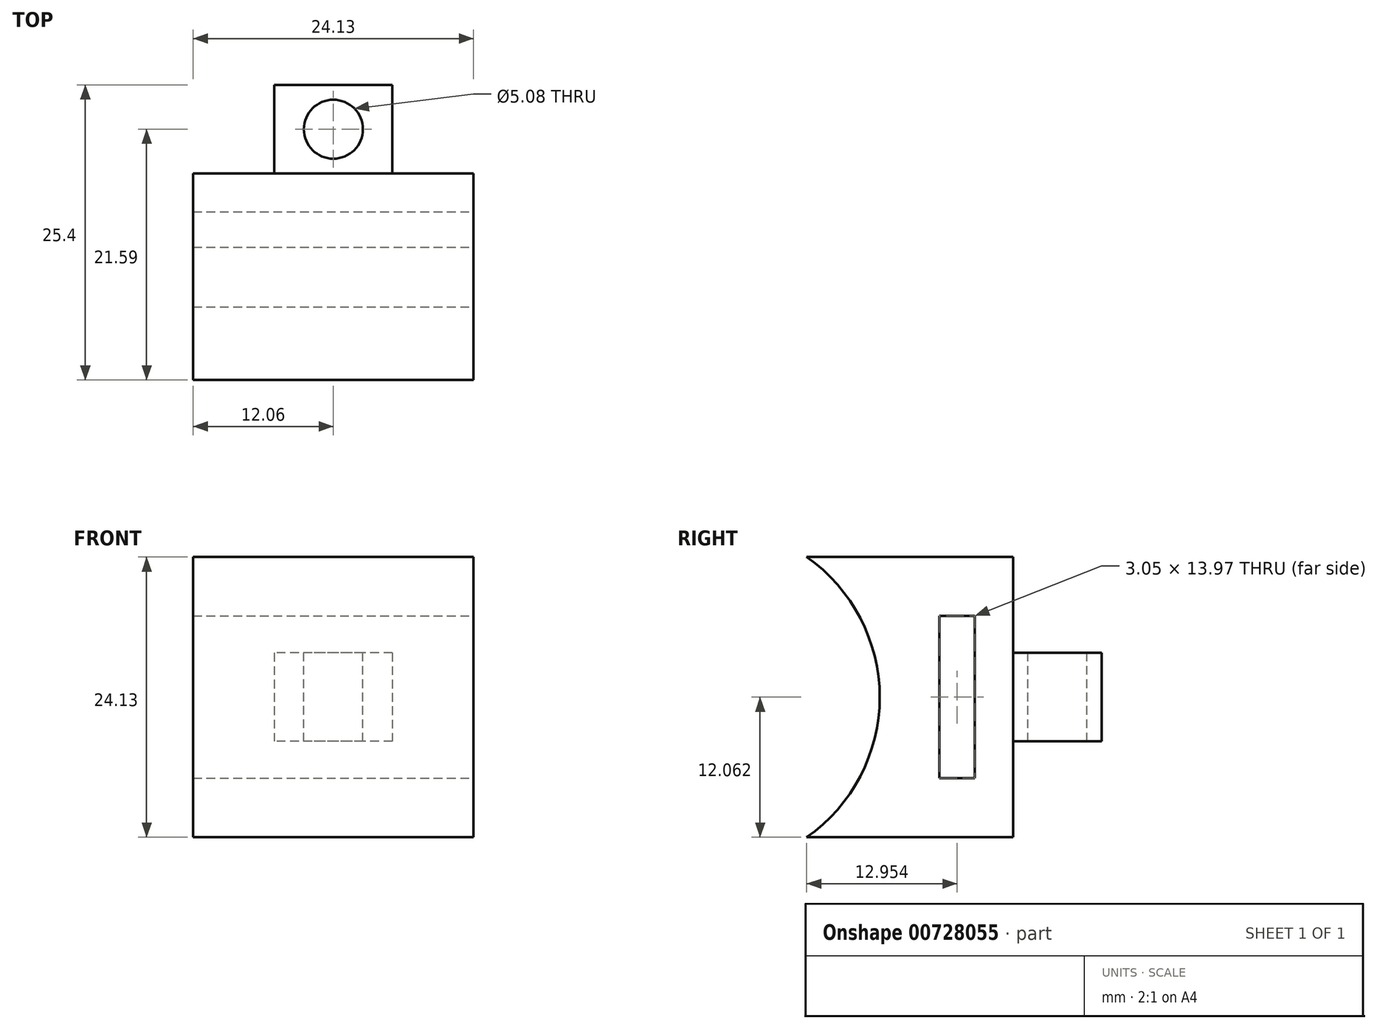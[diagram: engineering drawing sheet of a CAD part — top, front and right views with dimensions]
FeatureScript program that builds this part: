
annotation { "Feature Type Name" : "Feature", "Feature Type Description" : "" }
export const myFeature = defineFeature(function(context is Context, id is Id, definition is map)
    precondition{}
    {
        {
            var Q0;
            Q0=qCreatedBy(makeId("Front.planeOp"),FACE);
            var sketch = newSketch(context, id + "F0", { "sketchPlane" : qUnion([Q0])});
            skLineSegment(sketch, "E0.bottom", {"start": v(-34.91, 42.79) * mm, "end": v(-10.78, 42.79) * mm});
            skLineSegment(sketch, "E0.top", {"start": v(-34.91, 18.66) * mm, "end": v(-10.78, 18.66) * mm});
            skLineSegment(sketch, "E0.left", {"start": v(-34.91, 42.79) * mm, "end": v(-34.91, 18.66) * mm});
            skLineSegment(sketch, "E0.right", {"start": v(-10.78, 42.79) * mm, "end": v(-10.78, 18.66) * mm});
            skSolve(sketch);
        }
        {
            var Q0;
            Q0=makeQuery(id+"F0.imprint","IMPRINT",FACE,{"disambiguationData":[TD([[makeQuery(id+"F0.imprint","IMPRINT",EDGE,{"derivedFrom":sQuery(id+"F0.wireOp",EDGE,"E0.bottom")}),-1.0]])]});
            extrude(context, id + "F1", {"entities" : qUnion([Q0]), "depth" : 17.78 * mm, "offsetDistance" : 25.4 * mm});
        }
        {
            var Q0;
            Q0=makeQuery(id+"F1.opExtrude","SWEPT_FACE",FACE,{"disambiguationData":[OSD([sQuery(id+"F0.wireOp",EDGE,"E0.right")])]});
            var sketch = newSketch(context, id + "F2", { "sketchPlane" : qUnion([Q0])});
            skArc(sketch, "E1", {"start": v(-17.78, 18.66) * mm, "mid": v(-11.5, 30.72) * mm, "end": v(-17.78, 42.79) * mm});
            skSolve(sketch);
        }
        {
            var Q0;
            Q0 = qSketchRegion(id + "F2", true);
            var Q1;
            Q1=makeQuery(id+"F2.imprint","IMPRINT",FACE,{"disambiguationData":[TD([[makeQuery(id+"F2.imprint","IMPRINT",EDGE,{"derivedFrom":sQuery(id+"F2.wireOp",EDGE,"E1")}),1.0]])]});
            extrude(context, id + "F3", {"entities" : qUnion([Q0, Q1]), "operationType" : NewBodyOperationType.REMOVE, "endBound" : BoundingType.THROUGH_ALL, "oppositeDirection" : true, "depth" : 25.4 * mm, "offsetDistance" : 25.4 * mm});
        }
        {
            var Q0;
            Q0=makeQuery(id+"F1.opExtrude","CAP_FACE",FACE,{"disambiguationData":[OSD([sQuery(id+"F0.wireOp",EDGE,"E0.bottom"),sQuery(id+"F0.wireOp",EDGE,"E0.top"),sQuery(id+"F0.wireOp",EDGE,"E0.left"),sQuery(id+"F0.wireOp",EDGE,"E0.right")])],"isStart":true});
            var sketch = newSketch(context, id + "F4", { "sketchPlane" : qUnion([Q0])});
            skLineSegment(sketch, "E2.bottom", {"start": v(17.77, 34.53) * mm, "end": v(27.93, 34.53) * mm});
            skLineSegment(sketch, "E2.top", {"start": v(17.77, 26.91) * mm, "end": v(27.93, 26.91) * mm});
            skLineSegment(sketch, "E2.left", {"start": v(17.77, 34.53) * mm, "end": v(17.77, 26.91) * mm});
            skLineSegment(sketch, "E2.right", {"start": v(27.93, 34.53) * mm, "end": v(27.93, 26.91) * mm});
            skSolve(sketch);
        }
        {
            var Q0;
            Q0 = qSketchRegion(id + "F4", true);
            extrude(context, id + "F5", {"entities" : qUnion([Q0]), "operationType" : NewBodyOperationType.ADD, "depth" : 7.62 * mm, "offsetDistance" : 25.4 * mm});
        }
        {
            var Q0;
            Q0=makeQuery(id+"F5.opExtrude","SWEPT_FACE",FACE,{"disambiguationData":[OSD([sQuery(id+"F4.wireOp",EDGE,"E2.bottom")])]});
            var sketch = newSketch(context, id + "F6", { "sketchPlane" : qUnion([Q0])});
            skCircle(sketch, "E3", {"center": v(-22.85, 3.81) * mm, "radius": 2.54 * mm});
            skPoint(sketch, "E3.first.point", {"position": v(-21.78, 1.5) * mm});
            skPoint(sketch, "E3.second.point", {"position": v(-23.77, 6.18) * mm});
            skPoint(sketch, "E3.third.point", {"position": v(-25.37, 3.49) * mm});
            skSolve(sketch);
        }
        {
            var Q0;
            Q0=makeQuery(id+"F6.imprint","IMPRINT",FACE,{"disambiguationData":[TD([[makeQuery(id+"F6.imprint","IMPRINT",EDGE,{"derivedFrom":sQuery(id+"F6.wireOp",EDGE,"E3")}),1.0]])]});
            extrude(context, id + "F7", {"entities" : qUnion([Q0]), "operationType" : NewBodyOperationType.REMOVE, "endBound" : BoundingType.THROUGH_ALL, "oppositeDirection" : true, "depth" : 25.4 * mm, "offsetDistance" : 25.4 * mm});
        }
        {
            var Q0;
            Q0=makeQuery(id+"F1.opExtrude","SWEPT_FACE",FACE,{"disambiguationData":[OSD([sQuery(id+"F0.wireOp",EDGE,"E0.right")])]});
            var sketch = newSketch(context, id + "F8", { "sketchPlane" : qUnion([Q0])});
            skLineSegment(sketch, "E4.bottom", {"start": v(-6.35, 37.7) * mm, "end": v(-3.3, 37.7) * mm});
            skLineSegment(sketch, "E4.top", {"start": v(-6.35, 23.74) * mm, "end": v(-3.3, 23.74) * mm});
            skLineSegment(sketch, "E4.left", {"start": v(-6.35, 37.7) * mm, "end": v(-6.35, 23.74) * mm});
            skLineSegment(sketch, "E4.right", {"start": v(-3.3, 37.7) * mm, "end": v(-3.3, 23.74) * mm});
            skSolve(sketch);
        }
        {
            var Q0;
            Q0=makeQuery(id+"F8.imprint","IMPRINT",FACE,{"disambiguationData":[TD([[makeQuery(id+"F8.imprint","IMPRINT",EDGE,{"derivedFrom":sQuery(id+"F8.wireOp",EDGE,"E4.bottom")}),-1.0]])]});
            extrude(context, id + "F9", {"entities" : qUnion([Q0]), "operationType" : NewBodyOperationType.REMOVE, "endBound" : BoundingType.THROUGH_ALL, "oppositeDirection" : true, "depth" : 25.4 * mm, "offsetDistance" : 25.4 * mm});
        }
    });
